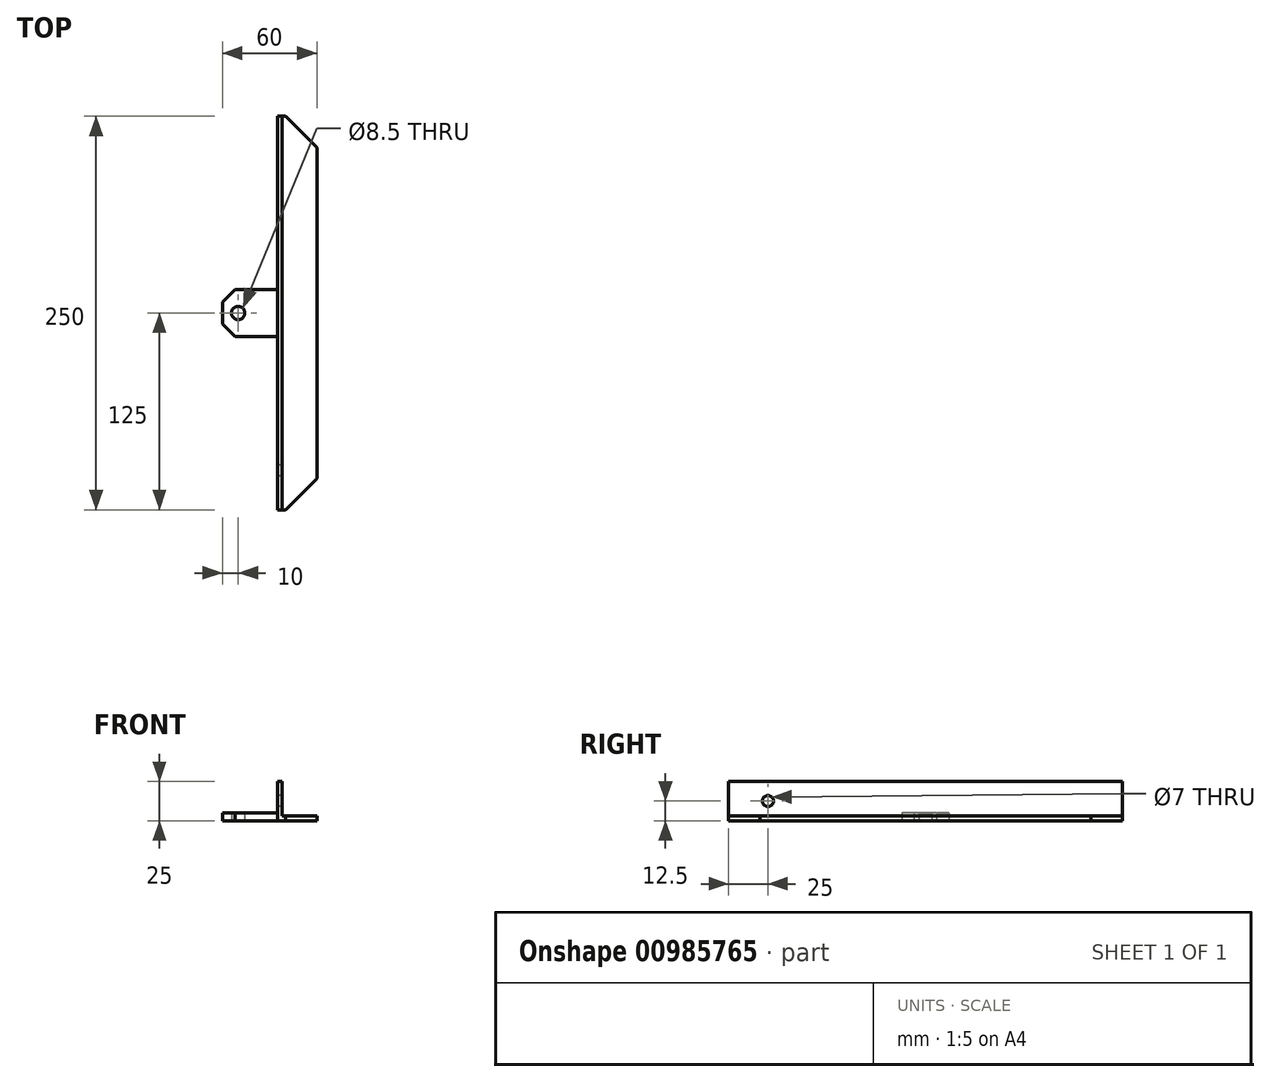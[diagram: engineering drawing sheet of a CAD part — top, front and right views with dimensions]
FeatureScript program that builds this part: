
annotation { "Feature Type Name" : "Feature", "Feature Type Description" : "" }
export const myFeature = defineFeature(function(context is Context, id is Id, definition is map)
    precondition{}
    {
        {
            var Q0;
            Q0=qCreatedBy(makeId("Front.planeOp"),FACE);
            var sketch = newSketch(context, id + "F0", { "sketchPlane" : qUnion([Q0])});
            skLineSegment(sketch, "E0.bottom", {"start": v(0, 0) * mm, "end": v(25, 0) * mm});
            skLineSegment(sketch, "E0.top", {"start": v(0, 25) * mm, "end": v(3, 25) * mm});
            skLineSegment(sketch, "E0.left", {"start": v(0, 0) * mm, "end": v(0, 25) * mm});
            skLineSegment(sketch, "E0.right", {"start": v(25, 0) * mm, "end": v(25, 3) * mm});
            skLineSegment(sketch, "E1", {"start": v(3, 25) * mm, "end": v(3, 3) * mm});
            skLineSegment(sketch, "E2", {"start": v(3, 3) * mm, "end": v(25, 3) * mm});
            skSolve(sketch);
        }
        {
            var Q0;
            Q0=makeQuery(id+"F0.imprint","IMPRINT",FACE,{"disambiguationData":[TD([[makeQuery(id+"F0.imprint","IMPRINT",EDGE,{"derivedFrom":sQuery(id+"F0.wireOp",EDGE,"E0.bottom")}),1.0]])]});
            extrude(context, id + "F1", {"entities" : qUnion([Q0]), "endBound" : BoundingType.SYMMETRIC, "depth" : 250 * mm, "offsetDistance" : 25 * mm});
        }
        {
            var Q0;
            Q0=makeQuery(id+"F1.opExtrude","CAP_EDGE",EDGE,{"disambiguationData":[OSD([sQuery(id+"F0.wireOp",EDGE,"E0.right")])],"isStart":false});
            var Q1;
            Q1=makeQuery(id+"F1.opExtrude","CAP_EDGE",EDGE,{"disambiguationData":[OSD([sQuery(id+"F0.wireOp",EDGE,"E0.right")])],"isStart":true});
            chamfer(context, id + "F2", {"entities" : qUnion([Q0, Q1]), "width" : 20 * mm, "tangentPropagation" : true});
        }
        {
            var Q0;
            Q0=qCreatedBy(makeId("Top.planeOp"),FACE);
            var sketch = newSketch(context, id + "F3", { "sketchPlane" : qUnion([Q0])});
            skLineSegment(sketch, "E3.bottom", {"start": v(0, 15) * mm, "end": v(-35, 15) * mm});
            skLineSegment(sketch, "E3.top", {"start": v(0, -15) * mm, "end": v(-35, -15) * mm});
            skLineSegment(sketch, "E3.left", {"start": v(0, 15) * mm, "end": v(0, -15) * mm});
            skLineSegment(sketch, "E3.right", {"start": v(-35, 15) * mm, "end": v(-35, -15) * mm});
            skCircle(sketch, "E4", {"center": v(-25, 0) * mm, "radius": 4.25 * mm});
            skSolve(sketch);
        }
        {
            var Q0;
            Q0=makeQuery(id+"F3.imprint","IMPRINT",FACE,{"disambiguationData":[TD([[makeQuery(id+"F3.imprint","IMPRINT",EDGE,{"derivedFrom":sQuery(id+"F3.wireOp",EDGE,"E3.bottom")}),1.0]])]});
            extrude(context, id + "F4", {"entities" : qUnion([Q0]), "operationType" : NewBodyOperationType.ADD, "depth" : 5 * mm, "offsetDistance" : 25 * mm});
        }
        {
            var Q0;
            Q0=makeQuery(id+"F4.opExtrude","SWEPT_EDGE",EDGE,{"disambiguationData":[OSD([sQuery(id+"F3.wireOp",EDGE,"E3.top"),sQuery(id+"F3.wireOp",EDGE,"E3.right")])]});
            var Q1;
            Q1=makeQuery(id+"F4.opExtrude","SWEPT_EDGE",EDGE,{"disambiguationData":[OSD([sQuery(id+"F3.wireOp",EDGE,"E3.bottom"),sQuery(id+"F3.wireOp",EDGE,"E3.right")])]});
            chamfer(context, id + "F5", {"entities" : qUnion([Q0, Q1]), "width" : 8 * mm, "tangentPropagation" : true});
        }
        {
            var Q0;
            Q0=qCreatedBy(makeId("Right.planeOp"),FACE);
            var sketch = newSketch(context, id + "F6", { "sketchPlane" : qUnion([Q0])});
            skCircle(sketch, "E5", {"center": v(-100, 12.5) * mm, "radius": 3.5 * mm});
            skCircle(sketch, "E6.MirrorC", {"center": v(100, 12.5) * mm, "radius": 3.5 * mm});
            skSolve(sketch);
        }
        {
            var Q0;
            Q0=makeQuery(id+"F6.imprint","IMPRINT",FACE,{"disambiguationData":[TD([[makeQuery(id+"F6.imprint","IMPRINT",EDGE,{"derivedFrom":sQuery(id+"F6.wireOp",EDGE,"E6.MirrorC")}),-1.0]])]});
            var Q1;
            Q1=makeQuery(id+"F6.imprint","IMPRINT",FACE,{"disambiguationData":[TD([[makeQuery(id+"F6.imprint","IMPRINT",EDGE,{"derivedFrom":sQuery(id+"F6.wireOp",EDGE,"E5")}),1.0]])]});
            extrude(context, id + "F7", {"entities" : qUnion([Q0, Q1]), "operationType" : NewBodyOperationType.REMOVE, "depth" : 25 * mm, "offsetDistance" : 25 * mm});
        }
    });
